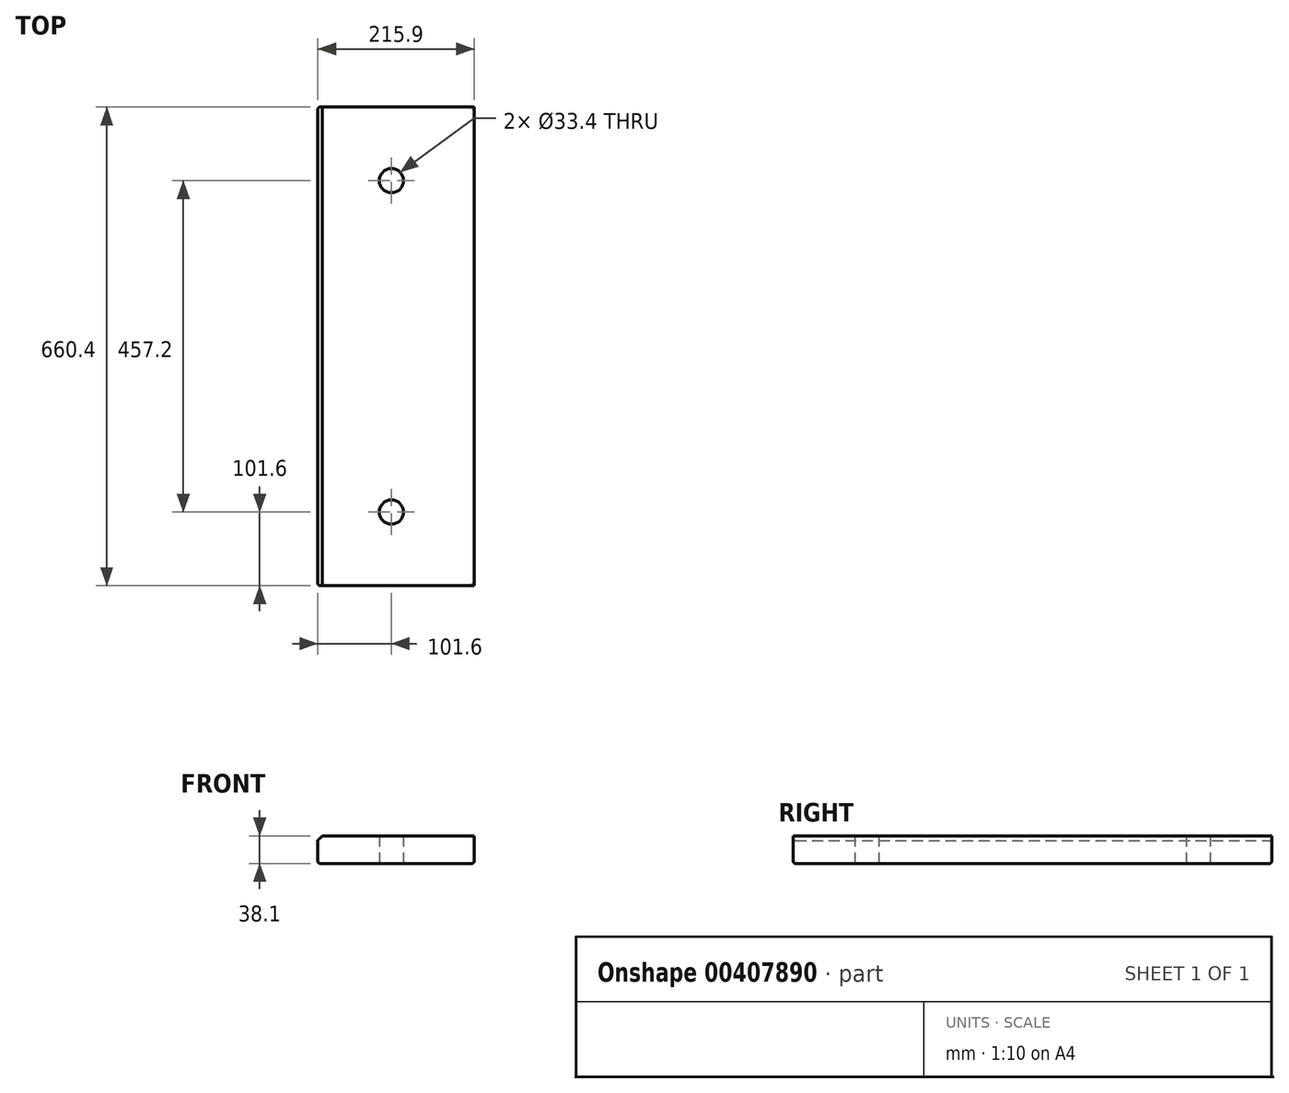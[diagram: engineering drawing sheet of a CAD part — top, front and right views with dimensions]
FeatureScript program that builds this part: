
annotation { "Feature Type Name" : "Feature", "Feature Type Description" : "" }
export const myFeature = defineFeature(function(context is Context, id is Id, definition is map)
    precondition{}
    {
        {
            var Q0;
            Q0=qCreatedBy(makeId("Top.planeOp"),FACE);
            var sketch = newSketch(context, id + "F0", { "sketchPlane" : qUnion([Q0])});
            skLineSegment(sketch, "E0.bottom", {"start": v(0, 0) * mm, "end": v(215.9, 0) * mm});
            skLineSegment(sketch, "E0.top", {"start": v(0, 660.4) * mm, "end": v(215.9, 660.4) * mm});
            skLineSegment(sketch, "E0.left", {"start": v(0, 0) * mm, "end": v(0, 660.4) * mm});
            skLineSegment(sketch, "E0.right", {"start": v(215.9, 0) * mm, "end": v(215.9, 660.4) * mm});
            skCircle(sketch, "E1", {"center": v(101.6, 558.8) * mm, "radius": 16.7 * mm});
            skCircle(sketch, "E2", {"center": v(101.6, 101.6) * mm, "radius": 16.7 * mm});
            skLineSegment(sketch, "E3", {"start": v(101.6, 558.8) * mm, "end": v(0, 558.8) * mm, "construction": true});
            skLineSegment(sketch, "E4", {"start": v(101.6, 558.8) * mm, "end": v(101.6, 660.4) * mm, "construction": true});
            skLineSegment(sketch, "E5", {"start": v(101.6, 0) * mm, "end": v(101.6, 101.6) * mm, "construction": true});
            skPoint(sketch, "E5.startSnap0", {"position": v(107.95, 0) * mm});
            skLineSegment(sketch, "E6", {"start": v(0, 101.6) * mm, "end": v(101.6, 101.6) * mm, "construction": true});
            skSolve(sketch);
        }
        {
            var Q0;
            Q0 = qSketchRegion(id + "F0", true);
            extrude(context, id + "F1", {"entities" : qUnion([Q0]), "depth" : 38.1 * mm});
        }
        {
            var Q0;
            Q0=makeQuery(id+"F1.opExtrude","CAP_EDGE",EDGE,{"disambiguationData":[OSD([sQuery(id+"F0.wireOp",EDGE,"E0.left")])],"isStart":false});
            chamfer(context, id + "F2", {"entities" : qUnion([Q0]), "width" : 6.35 * mm, "tangentPropagation" : true});
        }
        {
            var Q0;
            Q0=makeQuery(id+"F1.opExtrude","CAP_EDGE",EDGE,{"disambiguationData":[OSD([sQuery(id+"F0.wireOp",EDGE,"E0.right")])],"isStart":true});
            var Q1;
            Q1=makeQuery(id+"F1.opExtrude","CAP_EDGE",EDGE,{"disambiguationData":[OSD([sQuery(id+"F0.wireOp",EDGE,"E0.top")])],"isStart":true});
            var Q2;
            Q2=makeQuery(id+"F1.opExtrude","CAP_EDGE",EDGE,{"disambiguationData":[OSD([sQuery(id+"F0.wireOp",EDGE,"E0.bottom")])],"isStart":true});
            var Q3;
            Q3=makeQuery(id+"F1.opExtrude","CAP_EDGE",EDGE,{"disambiguationData":[OSD([sQuery(id+"F0.wireOp",EDGE,"E0.left")])],"isStart":true});
            var Q4;
            Q4=makeQuery(id+"F1.opExtrude","SWEPT_EDGE",EDGE,{"disambiguationData":[OSD([sQuery(id+"F0.wireOp",EDGE,"E0.bottom"),sQuery(id+"F0.wireOp",EDGE,"E0.left")])]});
            var Q5;
            Q5=makeQuery(id+"F1.opExtrude","SWEPT_EDGE",EDGE,{"disambiguationData":[OSD([sQuery(id+"F0.wireOp",EDGE,"E0.top"),sQuery(id+"F0.wireOp",EDGE,"E0.left")])]});
            fillet(context, id + "F3", {"entities" : qUnion([Q0, Q1, Q2, Q3, Q4, Q5]), "radius" : 3.17 * mm, "tangentPropagation" : true, "allowEdgeOverflow" : false});
        }
    });
